# Revit family: Saltwater Chlorinator - Power Pack
name_source: partatom
category: Mechanical Equipment
units: mm (PartAtom-declared; Revit-internal decimal feet)

## family parameters
Always vertical = Yes
Cut with Voids When Loaded = No
OmniClass Number = 23.75.00.00
OmniClass Title = Climate Control (HVAC)
Part Type = Normal
Room Calculation Point = No
Round Connector Dimension = Use Diameter
Shared = No
Work Plane-Based = No

## types (4) — shared parameters
Assembly Code = D2090400
Description = Jandy Commercial Saltwater Chlorinator
Fluidra_Cos ϕ = 100.00%
Fluidra_Description = Jandy Commercial Saltwater Chlorinator
Fluidra_Frequency = 60 Hz
Fluidra_Frequency2 = 50 Hz
Fluidra_Manufacturer = Fluidra
Fluidra_Voltage (High) = 240 V
Fluidra_Voltage (Low) = 120 V
Manufacturer = Fluidra
URL = https://www.jandy.com

## per-type parameters (varying)
| type | Fluidra_Amps_(120V) | Fluidra_Amps_(240V) | Heatsink |
| JSWC40 - Control Panel | 3 A | 2 A | No |
| JSWC53 - Control Panel | 4 A | 2 A | No |
| JSWC80 - Control Panel | 7 A | 3 A | Yes |
| JSWC100 - Control Panel | 7 A | 4 A | Yes |

note: column(s) folded — value = type name in every type: Fluidra_Model, Model

## geometry (parser evidence)
native form markers: Sweep x1
no freeform markers — native parametric forms only
